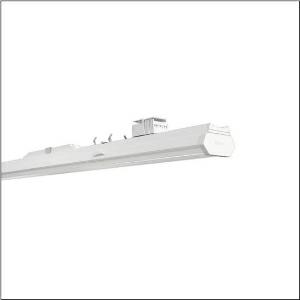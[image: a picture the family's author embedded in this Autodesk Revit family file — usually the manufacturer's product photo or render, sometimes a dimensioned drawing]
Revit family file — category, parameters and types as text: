
# Revit family: licross_21_protected_mo_52td12dn68xg
name_source: partatom
category: Lighting Fixtures
units: mm (PartAtom-declared; Revit-internal decimal feet)

## family parameters
Cut with Voids When Loaded = No
Host = Face
Light Source = No
Part Type = Normal
Room Calculation Point = No
Round Connector Dimension = Use Diameter
Shared = No

## types (1)
- --- (1 x LED, 8000 lm, 46.6 W, 6500K)
    Apparent Load = 47 VA
    CIE Flux Codes = 73 92 98 99 100
    Color Rendering = 80
    Color Temperature = 6500K
    Default Elevation = 1800 mm
    Description = Licross 21 Protected MO, luminaire insert, of sheet steel, galvanised, coil coated, white, length: 1.500mm, width: 90mm, height: 103mm, LED rated luminous flux: 8.000lm, light colour: 865, SDCM (Standard Deviation of Colour Matching)MacAdam ≤ 3 SDCM (initial), control gear: DALI 2, with plug, 5-pole, with phase selection, mains connection: 220..240V, AC, 50/60Hz, rated input power: 47W, internal wiring halogen-free, primary light control with lens, of plastic, primary optical cover: cover, of PMMA, light emission: direct distribution, primary light characteristic: symmetric, protection rating (complete): IP54, insulation class (complete): insulation class I (protective earthing), certification: CE, ENEC, VDE, UKCA, protection symbol: D if used in an environment with non-conductive dust loads with corresponding accessories, impact resistance: IK06, permissible ambient temperature for indoor applications: -25..+40°C, corresponds to IFS (International Featured Standards) requirements for safety and quality in the food industry, reducing of maximum allowable ambient temperature of 5°C with ceiling mounting, LABS conformity tested according to VDMA 24364:2018-05, The light source and the operating device comply with the requirements of the Ecodesign Regulation (EU) 2019/2020 and are replaceable in accordance with this regulation, packaging unit: 1 piece
    Height = 92 mm
    Lamp = 1 x LED
    Lamp Light Flux = 8000 lm
    Lamp Power = 46.6 W
    Lamp count = 1
    Length = 1500 mm
    Luminous efficacy = 172 lm/W
    Manufacturer = Siteco
    ModVariant = No
    Model = 52TD12DN68XG
    Mounting Place = Ceiling
    Mounting Type = Pendant
    Number of Poles = 1
    OnlyDefault = Yes
    Power Factor = 1
    Product Name = Licross 21 Protected MO
    Product group = luminaire insert | ceiling pendant
    ProductGroupID = 901
    Protection Class = Protection class I
    Protection Degree = IP 54
    RLX_Detail_Level = 1
    RLX_Emergency_Light_Flux = 0 lm
    RLX_Emergency_Type = 0
    RLX_Emergency_Type_DB = No
    RlxData = <blob elided: 24709 chars, md5=a18bd699>
    Socket = socket
    Standby Power = 0 W
    System Light Flux = 8000 lm
    System Power = 47 W
    Type Comments = factory setting: luminous flux: 100 % | dim-lin: 254 | 315 mA
    Type Image = l_1256148.jpg
    URL = http://relux.com
    VarID = @adj_037517
    Voltage = 0 V
    Weight = 0.00 kg
    Width = 88 mm

## geometry (parser evidence)
native form markers: Blend x4, Sweep x9
no freeform markers — native parametric forms only
